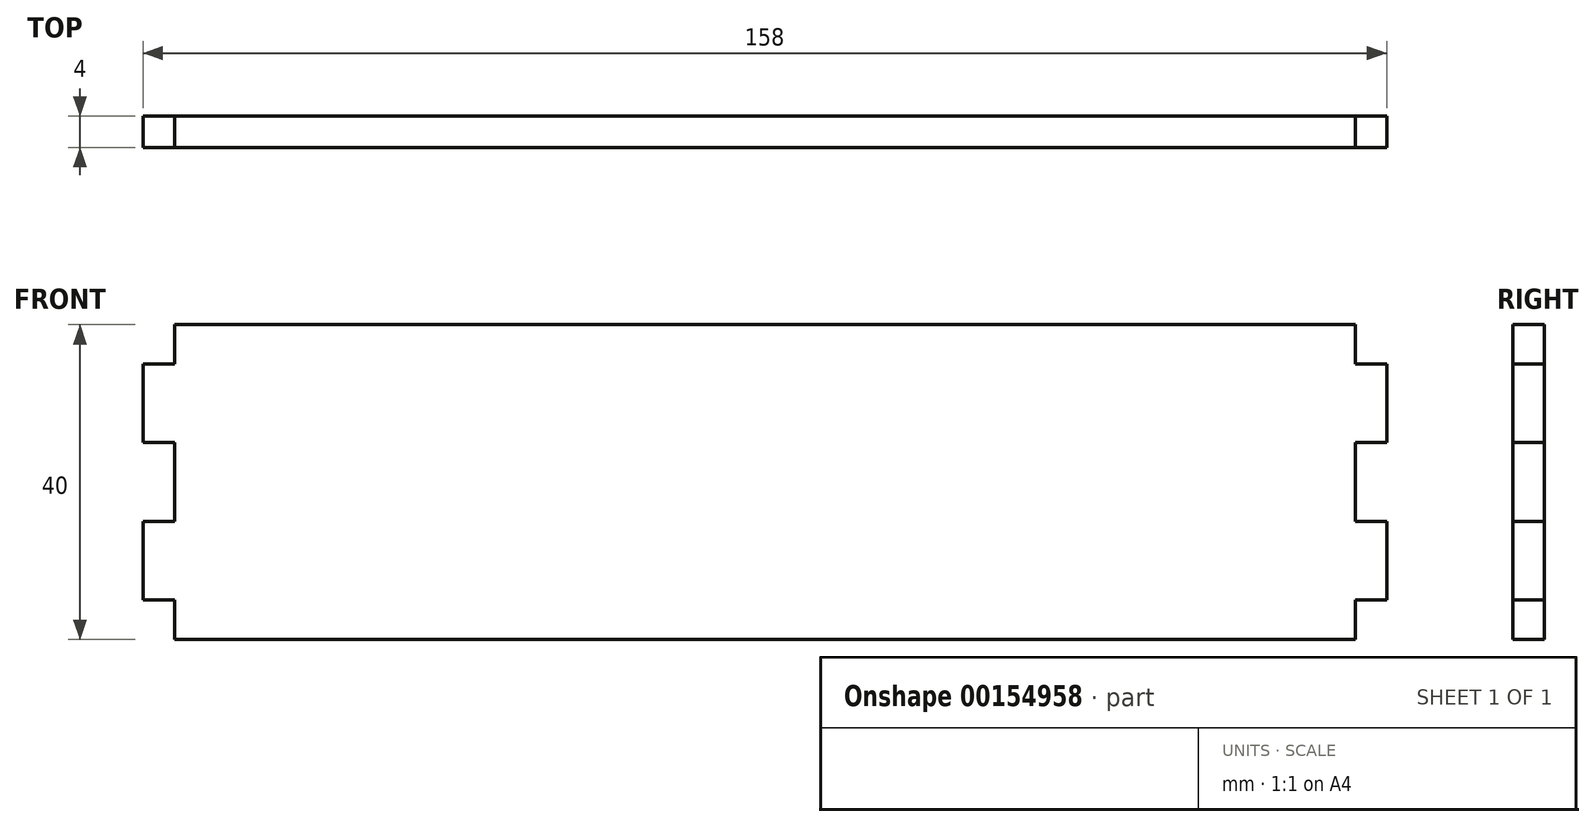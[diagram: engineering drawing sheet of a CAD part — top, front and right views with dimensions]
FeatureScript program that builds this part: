
annotation { "Feature Type Name" : "Feature", "Feature Type Description" : "" }
export const myFeature = defineFeature(function(context is Context, id is Id, definition is map)
    precondition{}
    {
        {
            var Q0;
            Q0=qCreatedBy(makeId("Front.planeOp"),FACE);
            var sketch = newSketch(context, id + "F0", { "sketchPlane" : qUnion([Q0])});
            skLineSegment(sketch, "E0.bottom", {"start": v(75, 20) * mm, "end": v(-75, 20) * mm});
            skLineSegment(sketch, "E0.top", {"start": v(75, -20) * mm, "end": v(-75, -20) * mm});
            skPoint(sketch, "E0.middle", {"position": v(0, 0) * mm});
            skLineSegment(sketch, "E1", {"start": v(0, 20) * mm, "end": v(0, 15.4) * mm});
            skPoint(sketch, "E1.endSnap0", {"position": v(0, 20) * mm});
            skPoint(sketch, "E2.end.orphan", {"position": v(-75, -5) * mm});
            skPoint(sketch, "E3.end.orphan", {"position": v(-79, -5) * mm});
            skPoint(sketch, "E3.start.orphan", {"position": v(-79, 5) * mm});
            skPoint(sketch, "E4.end.orphan", {"position": v(-75, 5) * mm});
            skPoint(sketch, "E4.start.orphan", {"position": v(-75, 0) * mm});
            skPoint(sketch, "E5.MirrorCS.start.orphan", {"position": v(79, -5) * mm});
            skPoint(sketch, "E6.MirrorCS.start.orphan", {"position": v(79, 5) * mm});
            skPoint(sketch, "E7.MirrorCS.start.orphan", {"position": v(75, 5) * mm});
            skPoint(sketch, "E8.orphan", {"position": v(75, -5) * mm});
            skLineSegment(sketch, "E9", {"start": v(-75, 20) * mm, "end": v(-75, 15) * mm});
            skLineSegment(sketch, "E10", {"start": v(-75, 15) * mm, "end": v(-79, 15) * mm});
            skLineSegment(sketch, "E11", {"start": v(-79, 15) * mm, "end": v(-79, 5) * mm});
            skLineSegment(sketch, "E12", {"start": v(-79, 5) * mm, "end": v(-75, 5) * mm});
            skLineSegment(sketch, "E13", {"start": v(-75, 5) * mm, "end": v(-75, -5) * mm});
            skLineSegment(sketch, "E14", {"start": v(-75, -5) * mm, "end": v(-79, -5) * mm});
            skLineSegment(sketch, "E15", {"start": v(-75, -20) * mm, "end": v(-75, -15) * mm});
            skLineSegment(sketch, "E16", {"start": v(-75, -15) * mm, "end": v(-79, -15) * mm});
            skLineSegment(sketch, "E17", {"start": v(-79, -15) * mm, "end": v(-79, -5) * mm});
            skLineSegment(sketch, "E18.MirrorCS", {"start": v(79, 5) * mm, "end": v(75, 5) * mm});
            skLineSegment(sketch, "E19.MirrorCS", {"start": v(75, -5) * mm, "end": v(79, -5) * mm});
            skLineSegment(sketch, "E20.MirrorCS", {"start": v(79, -15) * mm, "end": v(79, -5) * mm});
            skLineSegment(sketch, "E21.MirrorCS", {"start": v(75, 20) * mm, "end": v(75, 15) * mm});
            skLineSegment(sketch, "E22.MirrorCS", {"start": v(79, 15) * mm, "end": v(79, 5) * mm});
            skLineSegment(sketch, "E23.MirrorCS", {"start": v(75, -20) * mm, "end": v(75, -15) * mm});
            skLineSegment(sketch, "E24.MirrorCS", {"start": v(75, 15) * mm, "end": v(79, 15) * mm});
            skLineSegment(sketch, "E25.MirrorCS", {"start": v(75, -15) * mm, "end": v(79, -15) * mm});
            skPoint(sketch, "E26.MirrorP", {"position": v(75, 0) * mm});
            skLineSegment(sketch, "E27.MirrorCS", {"start": v(75, 5) * mm, "end": v(75, -5) * mm});
            skSolve(sketch);
        }
        {
            var Q0;
            Q0 = qSketchRegion(id + "F0", true);
            extrude(context, id + "F1", {"entities" : qUnion([Q0]), "depth" : 4 * mm});
        }
    });
